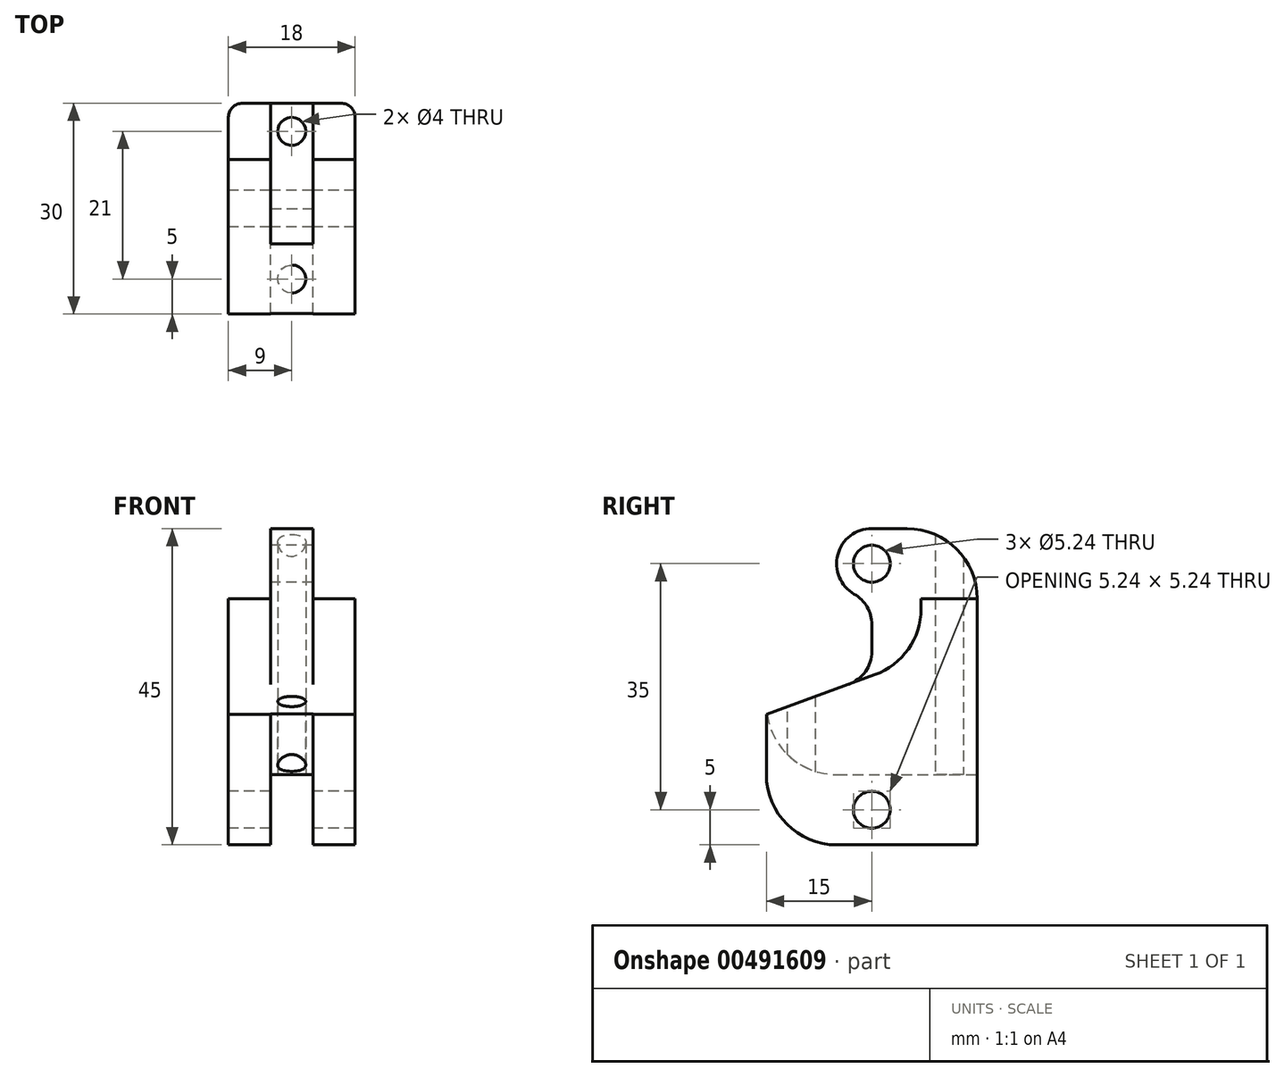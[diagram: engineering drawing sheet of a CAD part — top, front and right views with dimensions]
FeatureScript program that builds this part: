
annotation { "Feature Type Name" : "Feature", "Feature Type Description" : "" }
export const myFeature = defineFeature(function(context is Context, id is Id, definition is map)
    precondition{}
    {
        {
            var Q0;
            Q0=qCreatedBy(makeId("Front.planeOp"),FACE);
            var sketch = newSketch(context, id + "F0", { "sketchPlane" : qUnion([Q0])});
            skLineSegment(sketch, "E0.bottom", {"start": v(9, 12.5) * mm, "end": v(3, 12.5) * mm});
            skLineSegment(sketch, "E0.top", {"start": v(3, -12.5) * mm, "end": v(-3, -12.5) * mm});
            skLineSegment(sketch, "E0.left", {"start": v(9, 12.5) * mm, "end": v(9, -12.5) * mm});
            skLineSegment(sketch, "E0.right", {"start": v(-9, 12.5) * mm, "end": v(-9, -12.5) * mm});
            skPoint(sketch, "E0.middle", {"position": v(0, 0) * mm});
            skLineSegment(sketch, "E1.bottom", {"start": v(3, 22.5) * mm, "end": v(-3, 22.5) * mm});
            skLineSegment(sketch, "E1.left", {"start": v(3, 22.5) * mm, "end": v(3, 12.5) * mm});
            skLineSegment(sketch, "E1.right", {"start": v(-3, 22.5) * mm, "end": v(-3, 12.5) * mm});
            skPoint(sketch, "E1.middle", {"position": v(0, 12.5) * mm});
            skLineSegment(sketch, "E2.top", {"start": v(-9, -22.5) * mm, "end": v(-3, -22.5) * mm});
            skLineSegment(sketch, "E2.right", {"start": v(-3, -12.5) * mm, "end": v(-3, -22.5) * mm});
            skLineSegment(sketch, "E3.MirrorCS", {"start": v(3, -12.5) * mm, "end": v(3, -22.5) * mm});
            skLineSegment(sketch, "E4.MirrorCS", {"start": v(9, -22.5) * mm, "end": v(3, -22.5) * mm});
            skLineSegment(sketch, "E5.MirrorCS", {"start": v(9, -12.5) * mm, "end": v(9, -22.5) * mm});
            skLineSegment(sketch, "E6.trimOffspring", {"start": v(-3, 12.5) * mm, "end": v(-9, 12.5) * mm});
            skLineSegment(sketch, "E7", {"start": v(-9, -12.5) * mm, "end": v(-9, -22.5) * mm});
            skSolve(sketch);
        }
        {
            var Q0;
            Q0=makeQuery(id+"F0.imprint","IMPRINT",FACE,{"disambiguationData":[TD([[makeQuery(id+"F0.imprint","IMPRINT",EDGE,{"derivedFrom":sQuery(id+"F0.wireOp",EDGE,"E0.bottom")}),1.0]])]});
            extrude(context, id + "F1", {"entities" : qUnion([Q0]), "depth" : 30 * mm, "symmetric" : true});
        }
        {
            var Q0;
            Q0=makeQuery(id+"F1.opExtrude","SWEPT_FACE",FACE,{"disambiguationData":[OSD([sQuery(id+"F0.wireOp",EDGE,"E1.right")])]});
            var sketch = newSketch(context, id + "F2", { "sketchPlane" : qUnion([Q0])});
            skLineSegment(sketch, "E8", {"start": v(0, 12.5) * mm, "end": v(0, 22.5) * mm});
            skCircle(sketch, "E9", {"center": v(0, 17.5) * mm, "radius": 2.62 * mm});
            skSolve(sketch);
        }
        {
            var Q0;
            Q0=qSketchRegion(id+"F2",true);
            extrude(context, id + "F3", {"entities" : qUnion([Q0]), "operationType" : NewBodyOperationType.REMOVE, "oppositeDirection" : true, "depth" : 6 * mm});
        }
        {
            var Q0;
            Q0=makeQuery(id+"F1.opExtrude","SWEPT_FACE",FACE,{"disambiguationData":[OSD([sQuery(id+"F0.wireOp",EDGE,"E0.right"),sQuery(id+"F0.wireOp",EDGE,"E7")])]});
            var sketch = newSketch(context, id + "F4", { "sketchPlane" : qUnion([Q0])});
            skPoint(sketch, "E10.endSnap0", {"position": v(0, -22.5) * mm});
            skCircle(sketch, "E11", {"center": v(0, -17.5) * mm, "radius": 2.62 * mm});
            skLineSegment(sketch, "E12", {"start": v(0, -22.5) * mm, "end": v(0, -17.5) * mm});
            skSolve(sketch);
        }
        {
            var Q0;
            Q0=qSketchRegion(id+"F4",true);
            extrude(context, id + "F5", {"entities" : qUnion([Q0]), "operationType" : NewBodyOperationType.REMOVE, "oppositeDirection" : true, "depth" : 18 * mm});
        }
        {
            var Q0;
            Q0=makeQuery(id+"F1.opExtrude","CAP_EDGE",EDGE,{"disambiguationData":[OSD([sQuery(id+"F0.wireOp",EDGE,"E0.top")])],"isStart":false});
            fillet(context, id + "F6", {"entities" : qUnion([Q0]), "radius" : 10 * mm, "tangentPropagation" : true, "allowEdgeOverflow" : false});
        }
        {
            var Q0;
            Q0=makeQuery(id+"F1.opExtrude","CAP_EDGE",EDGE,{"disambiguationData":[OSD([sQuery(id+"F0.wireOp",EDGE,"E1.bottom")])],"isStart":true});
            var Q1;
            Q1=makeQuery(id+"F1.opExtrude","CAP_EDGE",EDGE,{"disambiguationData":[OSD([sQuery(id+"F0.wireOp",EDGE,"E1.bottom")])],"isStart":false});
            var Q2;
            Q2=makeQuery(id+"F1.opExtrude","CAP_EDGE",EDGE,{"disambiguationData":[OSD([sQuery(id+"F0.wireOp",EDGE,"E4.MirrorCS")])],"isStart":false});
            var Q3;
            Q3=makeQuery(id+"F1.opExtrude","CAP_EDGE",EDGE,{"disambiguationData":[OSD([sQuery(id+"F0.wireOp",EDGE,"E2.top")])],"isStart":false});
            fillet(context, id + "F7", {"entities" : qUnion([Q0, Q1, Q2, Q3]), "radius" : 10 * mm, "tangentPropagation" : true, "allowEdgeOverflow" : false});
        }
        {
            var Q0;
            Q0=makeQuery(id+"F1.opExtrude","SWEPT_FACE",FACE,{"disambiguationData":[OSD([sQuery(id+"F0.wireOp",EDGE,"E0.left"),sQuery(id+"F0.wireOp",EDGE,"E5.MirrorCS")])]});
            var sketch = newSketch(context, id + "F8", { "sketchPlane" : qUnion([Q0])});
            skPoint(sketch, "E13.endSnap0", {"position": v(0, 12.5) * mm});
            skLineSegment(sketch, "E14", {"start": v(-15, 12.5) * mm, "end": v(-15, -3.92) * mm});
            skLineSegment(sketch, "E15", {"start": v(-15, 12.5) * mm, "end": v(7, 12.5) * mm});
            skLineSegment(sketch, "E16", {"start": v(-15, -3.92) * mm, "end": v(15, -3.92) * mm});
            skLineSegment(sketch, "E17", {"start": v(-15, -3.92) * mm, "end": v(0.42, 1.7) * mm});
            skLineSegment(sketch, "E18", {"start": v(7, 12.5) * mm, "end": v(7, 11.09) * mm});
            skPoint(sketch, "E19.visualSharp", {"position": v(7, 4.09) * mm});
            skArc(sketch, "E19.filletArc", {"start": v(0.42, 1.7) * mm, "mid": v(5.2, 5.35) * mm, "end": v(7, 11.09) * mm});
            skSolve(sketch);
        }
        {
            var Q0;
            Q0=makeQuery(id+"F1.opExtrude","SWEPT_FACE",FACE,{"disambiguationData":[OSD([sQuery(id+"F0.wireOp",EDGE,"E0.right"),sQuery(id+"F0.wireOp",EDGE,"E7")])]});
            var sketch = newSketch(context, id + "F9", { "sketchPlane" : qUnion([Q0])});
            skLineSegment(sketch, "E20", {"start": v(-0.42, 1.7) * mm, "end": v(15, -3.92) * mm});
            skLineSegment(sketch, "E21", {"start": v(15, -3.92) * mm, "end": v(15, 12.5) * mm});
            skLineSegment(sketch, "E22", {"start": v(15, -3.92) * mm, "end": v(-15, -3.92) * mm});
            skLineSegment(sketch, "E23", {"start": v(15, 12.5) * mm, "end": v(-7, 12.5) * mm});
            skLineSegment(sketch, "E24", {"start": v(-7, 12.5) * mm, "end": v(-7, 11.09) * mm});
            skPoint(sketch, "E25.visualSharp", {"position": v(-7, 4.09) * mm});
            skArc(sketch, "E25.filletArc", {"start": v(-7, 11.09) * mm, "mid": v(-5.2, 5.35) * mm, "end": v(-0.42, 1.7) * mm});
            skSolve(sketch);
        }
        {
            var Q0;
            Q0=makeQuery(id+"F9.imprint","IMPRINT",FACE,{"disambiguationData":[TD([[makeQuery(id+"F9.imprint","IMPRINT",EDGE,{"derivedFrom":sQuery(id+"F9.wireOp",EDGE,"E20")}),1.0]])]});
            extrude(context, id + "F10", {"entities" : qUnion([Q0]), "operationType" : NewBodyOperationType.REMOVE, "oppositeDirection" : true, "depth" : 6 * mm});
        }
        {
            var Q0;
            Q0=makeQuery(id+"F8.imprint","IMPRINT",FACE,{"disambiguationData":[TD([[makeQuery(id+"F8.imprint","IMPRINT",EDGE,{"derivedFrom":sQuery(id+"F8.wireOp",EDGE,"E14")}),1.0]])]});
            extrude(context, id + "F11", {"entities" : qUnion([Q0]), "operationType" : NewBodyOperationType.REMOVE, "oppositeDirection" : true, "depth" : 6 * mm});
        }
        {
            var Q0;
            Q0=makeQuery(id+"F1.opExtrude","CAP_EDGE",EDGE,{"disambiguationData":[OSD([sQuery(id+"F0.wireOp",EDGE,"E0.left"),sQuery(id+"F0.wireOp",EDGE,"E5.MirrorCS")])],"isStart":true});
            var Q1;
            Q1=makeQuery(id+"F1.opExtrude","CAP_EDGE",EDGE,{"disambiguationData":[OSD([sQuery(id+"F0.wireOp",EDGE,"E0.right"),sQuery(id+"F0.wireOp",EDGE,"E7")])],"isStart":true});
            fillet(context, id + "F12", {"entities" : qUnion([Q0, Q1]), "radius" : 2 * mm, "tangentPropagation" : true, "allowEdgeOverflow" : false});
        }
        {
            var Q0;
            Q0=makeQuery(id+"F10.boolean.opBoolean","MERGE",FACE,{"derivedFrom":[makeQuery(id+"F1.opExtrude","SWEPT_FACE",FACE,{"disambiguationData":[OSD([sQuery(id+"F0.wireOp",EDGE,"E1.right")])]}),makeQuery(id+"F10.opExtrude","CAP_FACE",FACE,{"disambiguationData":[OSD([sQuery(id+"F9.wireOp",EDGE,"E20"),sQuery(id+"F9.wireOp",EDGE,"E21"),sQuery(id+"F9.wireOp",EDGE,"E23"),sQuery(id+"F9.wireOp",EDGE,"E24"),sQuery(id+"F9.wireOp",EDGE,"E25.filletArc")])],"isStart":false})]});
            var sketch = newSketch(context, id + "F13", { "sketchPlane" : qUnion([Q0])});
            skLineSegment(sketch, "E26", {"start": v(0, 22.5) * mm, "end": v(0, 20.12) * mm});
            skCircle(sketch, "E27", {"center": v(0, 17.5) * mm, "radius": 5 * mm});
            skLineSegment(sketch, "E28", {"start": v(0, 17.5) * mm, "end": v(5, 17.5) * mm});
            skLineSegment(sketch, "E29", {"start": v(5, 17.5) * mm, "end": v(5, -0.28) * mm});
            skSolve(sketch);
        }
        {
            var Q0;
            {var subQ1=sQuery(id+"F13.wireOp",EDGE,"E29");Q0=makeQuery(id+"F13.imprint","IMPRINT",FACE,{"disambiguationData":[TD([[makeQuery(id+"F13.imprint","IMPRINT",EDGE,{"derivedFrom":subQ1}),1.0]])]});}
            extrude(context, id + "F14", {"entities" : qUnion([Q0]), "operationType" : NewBodyOperationType.REMOVE, "oppositeDirection" : true, "depth" : 6 * mm});
        }
        {
            var Q0;
            Q0=makeQuery(id+"F1.opExtrude","SWEPT_FACE",FACE,{"disambiguationData":[OSD([sQuery(id+"F0.wireOp",EDGE,"E0.top")])]});
            var sketch = newSketch(context, id + "F15", { "sketchPlane" : qUnion([Q0])});
            skSolve(sketch);
        }
        {
            var Q0;
            Q0=makeQuery(id+"F14.boolean.opBoolean","COPY",EDGE,{"derivedFrom":makeQuery(id+"F14.opExtrude","SWEPT_EDGE",EDGE,{"disambiguationData":[OSD([sQuery(id+"F13.wireOp",EDGE,"E27"),sQuery(id+"F13.wireOp",EDGE,"E28"),sQuery(id+"F13.wireOp",EDGE,"E29")])]})});
            cPlane(context, id + "F16", {"entities" : qUnion([Q0]), "cplaneType" : CPlaneType.LINE_ANGLE, "offset" : 25 * mm, "angle" : 90 * degree, "width" : 150 * mm, "height" : 150 * mm});
        }
        {
            var Q0;
            Q0=qCreatedBy(id+"F16.planeOp",FACE);
            var sketch = newSketch(context, id + "F17", { "sketchPlane" : qUnion([Q0])});
            skLineSegment(sketch, "E30", {"start": v(0, -5) * mm, "end": v(0, -15) * mm});
            skCircle(sketch, "E31", {"center": v(0, -10) * mm, "radius": 2 * mm});
            skSolve(sketch);
        }
        {
            var Q0;
            {var subQ0=sQuery(id+"F17.wireOp",EDGE,"E31");var subQ1=sQuery(id+"F17.wireOp",EDGE,"E30");var subQ2=makeQuery(id+"F17.imprint","INTERSECT",VERTEX,{"disambiguationData":[OD(0.0)],"derivedFrom":[subQ1,subQ0]});Q0=makeQuery(id+"F17.imprint","IMPRINT",FACE,{"disambiguationData":[TD([[makeQuery(id+"F17.imprint","IMPRINT",EDGE,{"disambiguationData":[TD([[subQ2,1.0]])],"derivedFrom":subQ1}),-1.0]])]});}
            var Q1;
            {var subQ0=sQuery(id+"F17.wireOp",EDGE,"E31");var subQ1=sQuery(id+"F17.wireOp",EDGE,"E30");var subQ2=makeQuery(id+"F17.imprint","INTERSECT",VERTEX,{"disambiguationData":[OD(0.0)],"derivedFrom":[subQ1,subQ0]});Q1=makeQuery(id+"F17.imprint","IMPRINT",FACE,{"disambiguationData":[TD([[makeQuery(id+"F17.imprint","IMPRINT",EDGE,{"disambiguationData":[TD([[subQ2,1.0]])],"derivedFrom":subQ1}),1.0]])]});}
            extrude(context, id + "F18", {"entities" : qUnion([Q0, Q1]), "operationType" : NewBodyOperationType.REMOVE, "oppositeDirection" : true, "depth" : 40 * mm});
        }
        {
            var Q0;
            {var subQ0=sQuery(id+"F0.wireOp",EDGE,"E0.top");Q0=makeQuery(id+"F15.imprint","IMPRINT",FACE,{"disambiguationData":[TD([[makeQuery(id+"F15.imprint","IMPRINT",EDGE,{"derivedFrom":makeQuery(id+"F1.opExtrude","CAP_EDGE",EDGE,{"disambiguationData":[OSD([subQ0])],"isStart":true})}),-1.0]])]});}
            var sketch = newSketch(context, id + "F19", { "sketchPlane" : qUnion([Q0])});
            skLineSegment(sketch, "E32", {"start": v(0, -11) * mm, "end": v(0, -15) * mm});
            skCircle(sketch, "E33", {"center": v(0, -11) * mm, "radius": 2 * mm});
            skLineSegment(sketch, "E34", {"start": v(0, -11) * mm, "end": v(0, 0) * mm});
            skSolve(sketch);
        }
        {
            var Q0;
            Q0 = qSketchRegion(id + "F19", true);
            extrude(context, id + "F20", {"entities" : qUnion([Q0]), "operationType" : NewBodyOperationType.REMOVE, "oppositeDirection" : true, "depth" : 40 * mm});
        }
        {
            var Q0;
            Q0=makeQuery(id+"F11.boolean.opBoolean","MERGE",FACE,{"derivedFrom":[makeQuery(id+"F1.opExtrude","SWEPT_FACE",FACE,{"disambiguationData":[OSD([sQuery(id+"F0.wireOp",EDGE,"E1.left")])]}),makeQuery(id+"F11.opExtrude","CAP_FACE",FACE,{"disambiguationData":[OSD([sQuery(id+"F8.wireOp",EDGE,"E14"),sQuery(id+"F8.wireOp",EDGE,"E15"),sQuery(id+"F8.wireOp",EDGE,"E17"),sQuery(id+"F8.wireOp",EDGE,"E18"),sQuery(id+"F8.wireOp",EDGE,"E19.filletArc")])],"isStart":false})]});
            var sketch = newSketch(context, id + "F21", { "sketchPlane" : qUnion([Q0])});
            skArc(sketch, "E35", {"start": v(-5, 17.5) * mm, "mid": v(-3.54, 13.96) * mm, "end": v(0, 12.5) * mm});
            skLineSegment(sketch, "E36", {"start": v(0, 12.5) * mm, "end": v(0, 1.54) * mm});
            skLineSegment(sketch, "E37", {"start": v(0, 1.54) * mm, "end": v(-5, -0.28) * mm});
            skLineSegment(sketch, "E38", {"start": v(-5, -0.28) * mm, "end": v(-5, 17.5) * mm});
            skSolve(sketch);
        }
        {
            var Q0;
            Q0=makeQuery(id+"F21.imprint","IMPRINT",FACE,{"disambiguationData":[TD([[makeQuery(id+"F21.imprint","IMPRINT",EDGE,{"derivedFrom":sQuery(id+"F21.wireOp",EDGE,"E35")}),-1.0]])]});
            extrude(context, id + "F22", {"entities" : qUnion([Q0]), "operationType" : NewBodyOperationType.REMOVE, "oppositeDirection" : true, "depth" : 6 * mm});
        }
        {
            var Q0;
            Q0=makeQuery(id+"F22.boolean.opBoolean","COPY",EDGE,{"derivedFrom":makeQuery(id+"F22.opExtrude","SWEPT_EDGE",EDGE,{"disambiguationData":[OSD([sQuery(id+"F21.wireOp",EDGE,"E35"),sQuery(id+"F21.wireOp",EDGE,"E36")])]})});
            var Q1;
            Q1=makeQuery(id+"F22.boolean.opBoolean","COPY",EDGE,{"derivedFrom":makeQuery(id+"F22.opExtrude","SWEPT_EDGE",EDGE,{"disambiguationData":[OSD([sQuery(id+"F8.wireOp",EDGE,"E17"),sQuery(id+"F21.wireOp",EDGE,"E36"),sQuery(id+"F21.wireOp",EDGE,"E37")])]})});
            fillet(context, id + "F23", {"entities" : qUnion([Q0, Q1]), "radius" : 5 * mm, "tangentPropagation" : true, "allowEdgeOverflow" : false});
        }
    });
